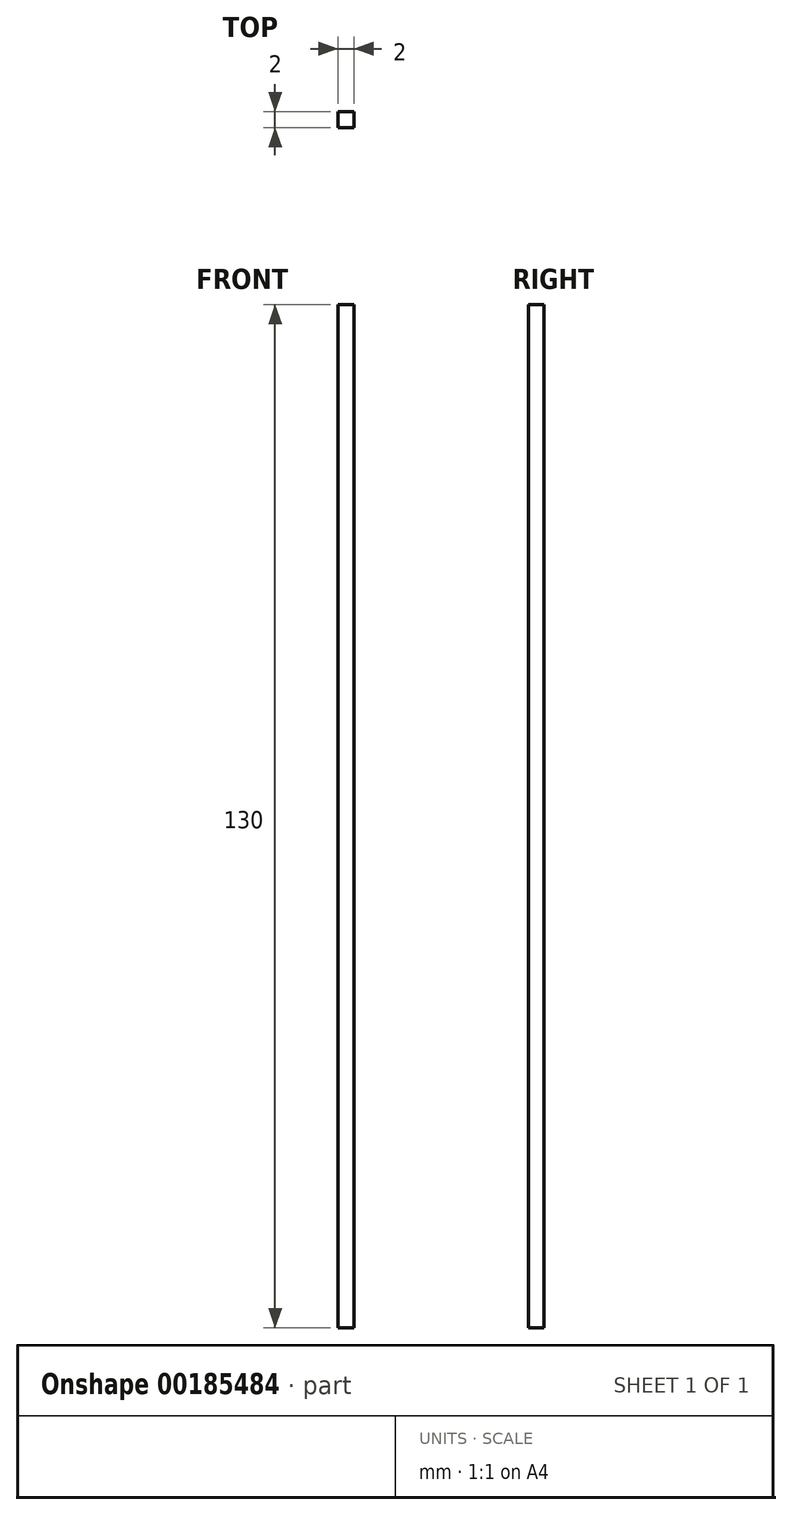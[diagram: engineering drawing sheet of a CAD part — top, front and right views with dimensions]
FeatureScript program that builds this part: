
annotation { "Feature Type Name" : "Feature", "Feature Type Description" : "" }
export const myFeature = defineFeature(function(context is Context, id is Id, definition is map)
    precondition{}
    {
        {
            var Q0;
            Q0=qCreatedBy(makeId("Top.planeOp"),FACE);
            var sketch = newSketch(context, id + "F0", { "sketchPlane" : qUnion([Q0])});
            skLineSegment(sketch, "E0.bottom", {"start": v(0, 0) * mm, "end": v(-2, 0) * mm});
            skLineSegment(sketch, "E0.top", {"start": v(0, 2) * mm, "end": v(-2, 2) * mm});
            skLineSegment(sketch, "E0.left", {"start": v(0, 0) * mm, "end": v(0, 2) * mm});
            skLineSegment(sketch, "E0.right", {"start": v(-2, 0) * mm, "end": v(-2, 2) * mm});
            skSolve(sketch);
        }
        {
            var Q0;
            Q0 = qSketchRegion(id + "F0", true);
            extrude(context, id + "F1", {"entities" : qUnion([Q0]), "depth" : 130 * mm});
        }
    });
